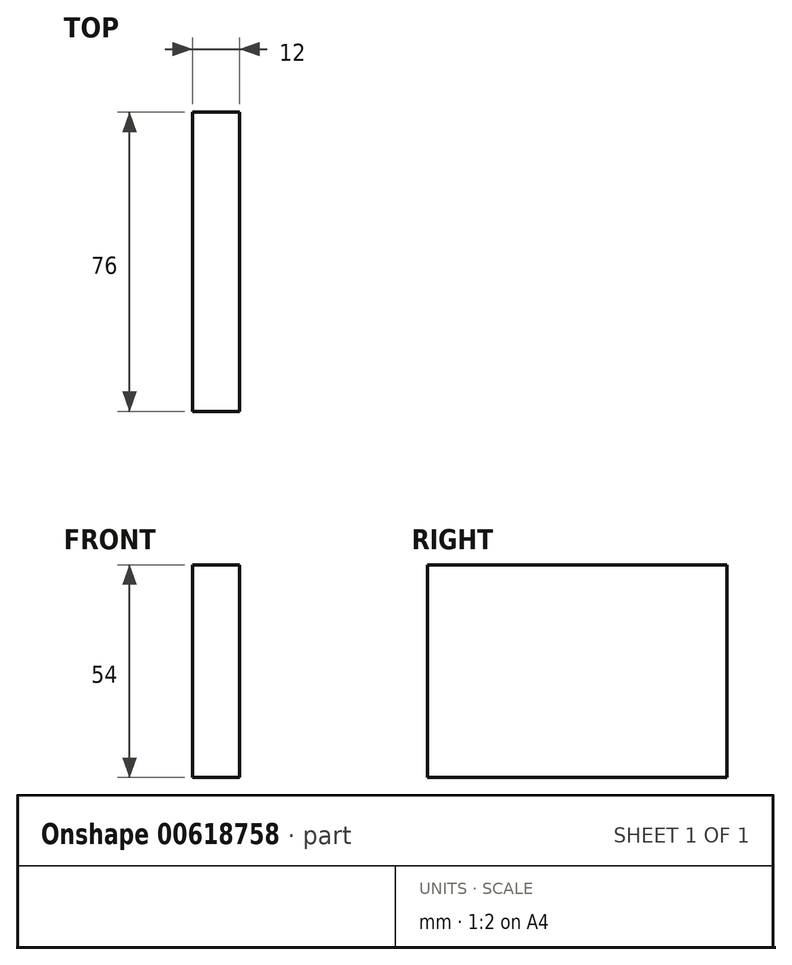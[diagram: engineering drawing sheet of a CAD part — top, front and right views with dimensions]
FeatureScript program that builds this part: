
annotation { "Feature Type Name" : "Feature", "Feature Type Description" : "" }
export const myFeature = defineFeature(function(context is Context, id is Id, definition is map)
    precondition{}
    {
        {
            var Q0;
            Q0=qCreatedBy(makeId("Front.planeOp"),FACE);
            var sketch = newSketch(context, id + "F0", { "sketchPlane" : qUnion([Q0])});
            skLineSegment(sketch, "E0.bottom", {"start": v(6, -27) * mm, "end": v(-6, -27) * mm});
            skLineSegment(sketch, "E0.top", {"start": v(6, 27) * mm, "end": v(-6, 27) * mm});
            skLineSegment(sketch, "E0.left", {"start": v(6, -27) * mm, "end": v(6, 27) * mm});
            skLineSegment(sketch, "E0.right", {"start": v(-6, -27) * mm, "end": v(-6, 27) * mm});
            skPoint(sketch, "E0.middle", {"position": v(0, 0) * mm});
            skSolve(sketch);
        }
        {
            var Q0;
            Q0=makeQuery(id+"F0.imprint","IMPRINT",FACE,{"disambiguationData":[TD([[makeQuery(id+"F0.imprint","IMPRINT",EDGE,{"derivedFrom":sQuery(id+"F0.wireOp",EDGE,"E0.bottom")}),-1.0]])]});
            extrude(context, id + "F1", {"entities" : qUnion([Q0]), "depth" : 76 * mm, "offsetDistance" : 25 * mm});
        }
    });
